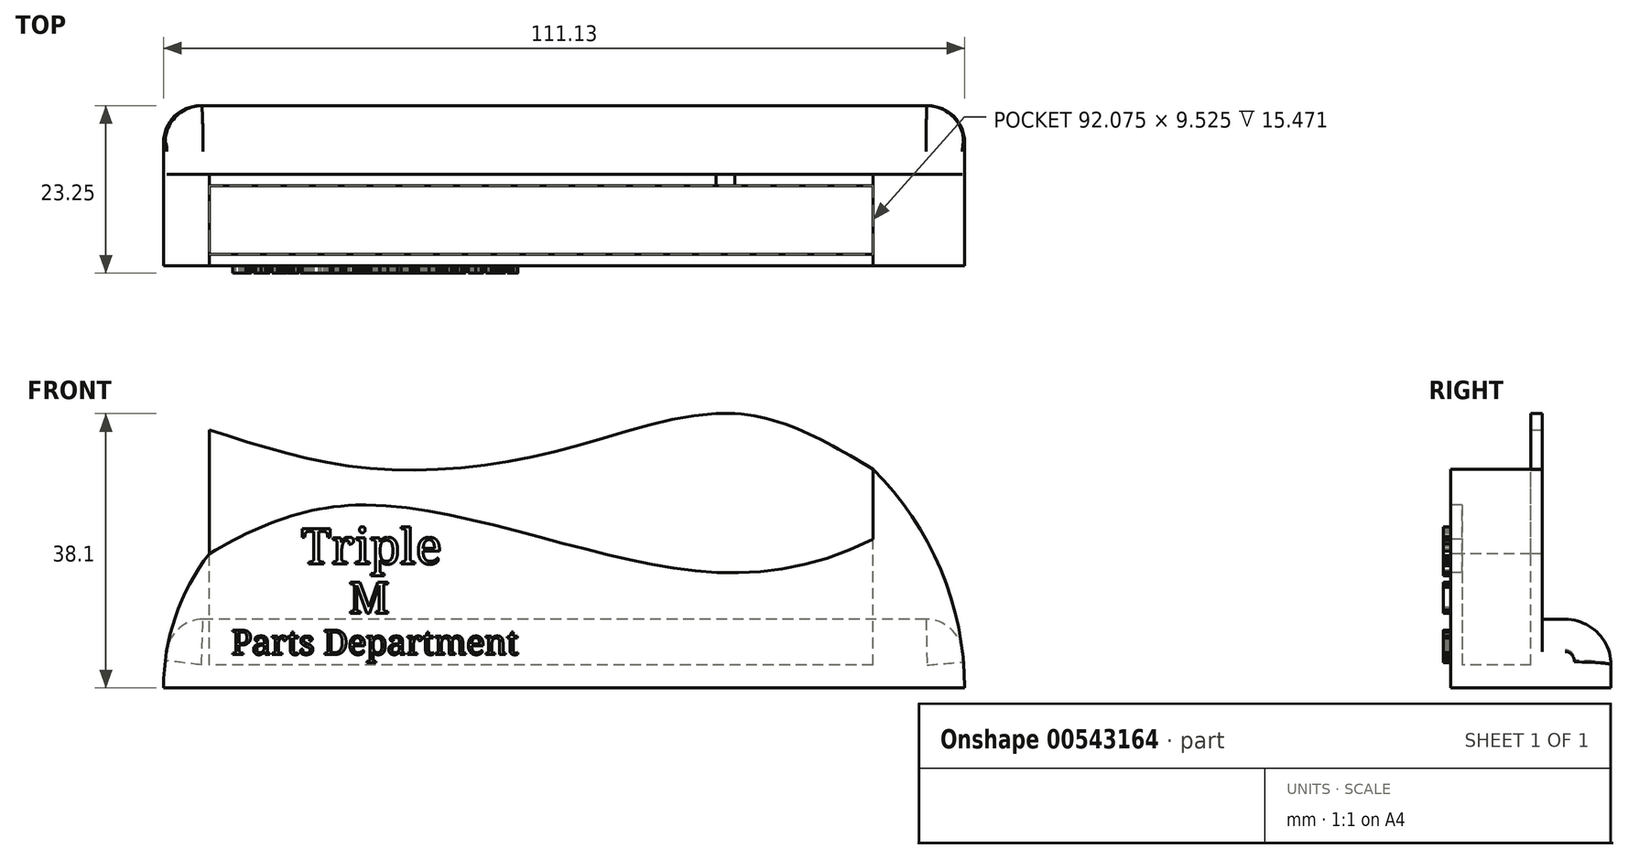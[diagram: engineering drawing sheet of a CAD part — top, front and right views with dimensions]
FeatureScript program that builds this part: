
annotation { "Feature Type Name" : "Feature", "Feature Type Description" : "" }
export const myFeature = defineFeature(function(context is Context, id is Id, definition is map)
    precondition{}
    {
        {
            var Q0;
            Q0=qCreatedBy(makeId("Right.planeOp"),FACE);
            var sketch = newSketch(context, id + "F0", { "sketchPlane" : qUnion([Q0])});
            skLineSegment(sketch, "E0", {"start": v(0, 0) * mm, "end": v(0, 25.4) * mm});
            skLineSegment(sketch, "E1", {"start": v(0, 25.4) * mm, "end": v(1.59, 25.4) * mm});
            skLineSegment(sketch, "E2", {"start": v(1.59, 25.4) * mm, "end": v(1.59, 3.18) * mm});
            skLineSegment(sketch, "E3", {"start": v(1.59, 3.18) * mm, "end": v(11.11, 3.18) * mm});
            skLineSegment(sketch, "E4", {"start": v(11.11, 3.18) * mm, "end": v(11.11, 38.1) * mm});
            skLineSegment(sketch, "E5", {"start": v(11.11, 38.1) * mm, "end": v(12.7, 38.1) * mm});
            skLineSegment(sketch, "E6", {"start": v(12.7, 38.1) * mm, "end": v(12.7, 0) * mm});
            skLineSegment(sketch, "E7", {"start": v(12.7, 0) * mm, "end": v(0, 0) * mm});
            skSolve(sketch);
        }
        {
            var Q0;
            Q0=makeQuery(id+"F0.imprint","IMPRINT",FACE,{"disambiguationData":[TD([[makeQuery(id+"F0.imprint","IMPRINT",EDGE,{"derivedFrom":sQuery(id+"F0.wireOp",EDGE,"E0")}),-1.0]])]});
            extrude(context, id + "F1", {"entities" : qUnion([Q0]), "depth" : 92.07 * mm});
        }
        {
            var Q0;
            Q0=makeQuery(id+"F1.opExtrude","SWEPT_FACE",FACE,{"disambiguationData":[OSD([sQuery(id+"F0.wireOp",EDGE,"E0")])]});
            var sketch = newSketch(context, id + "F2", { "sketchPlane" : qUnion([Q0])});
            skFitSpline(sketch, "E8", {"points": [v(0, 18.6) * mm, v(21.38, 25.4) * mm, v(56.78, 18.13) * mm, v(92.08, 20.65) * mm], "startDerivative": vector(67.88, 41.03) * mm, "endDerivative": vector(105.85, 52.89) * mm});
            skSolve(sketch);
        }
        {
            var Q0;
            {var subQ0=sQuery(id+"F0.wireOp",EDGE,"E0");var subQ1=makeQuery(id+"F1.opExtrude","CAP_EDGE",EDGE,{"disambiguationData":[OSD([subQ0])],"isStart":true});var subQ2=sQuery(id+"F2.wireOp",EDGE,"E8");var subQ3=makeQuery(id+"F2.imprint","INTERSECT",VERTEX,{"derivedFrom":[subQ1,subQ2]});Q0=makeQuery(id+"F2.imprint","IMPRINT",FACE,{"disambiguationData":[TD([[makeQuery(id+"F2.imprint","IMPRINT",EDGE,{"disambiguationData":[TD([[subQ3,-1.0]])],"derivedFrom":subQ2}),1.0]])]});}
            var Q1;
            {var subQ0=sQuery(id+"F0.wireOp",EDGE,"E0");var subQ1=makeQuery(id+"F1.opExtrude","CAP_EDGE",EDGE,{"disambiguationData":[OSD([subQ0])],"isStart":false});var subQ2=sQuery(id+"F2.wireOp",EDGE,"E8");var subQ3=makeQuery(id+"F2.imprint","INTERSECT",VERTEX,{"derivedFrom":[subQ1,subQ2]});Q1=makeQuery(id+"F2.imprint","IMPRINT",FACE,{"disambiguationData":[TD([[makeQuery(id+"F2.imprint","IMPRINT",EDGE,{"disambiguationData":[TD([[subQ3,1.0]])],"derivedFrom":subQ2}),1.0]])]});}
            extrude(context, id + "F3", {"entities" : qUnion([Q0, Q1]), "operationType" : NewBodyOperationType.REMOVE, "endBound" : BoundingType.UP_TO_NEXT, "oppositeDirection" : true, "depth" : 25.4 * mm});
        }
        {
            var Q0;
            Q0=makeQuery(id+"F1.opExtrude","SWEPT_FACE",FACE,{"disambiguationData":[OSD([sQuery(id+"F0.wireOp",EDGE,"E6")])]});
            var sketch = newSketch(context, id + "F4", { "sketchPlane" : qUnion([Q0])});
            skFitSpline(sketch, "E9", {"points": [v(-92.08, 30.36) * mm, v(-72.87, 38.1) * mm, v(-46.83, 32.53) * mm, v(-20.34, 30.7) * mm, v(0, 35.84) * mm], "startDerivative": vector(78.4, 47.13) * mm, "endDerivative": vector(83.06, 27.16) * mm});
            skSolve(sketch);
        }
        {
            var Q0;
            {var subQ0=sQuery(id+"F0.wireOp",EDGE,"E6");var subQ1=makeQuery(id+"F1.opExtrude","CAP_EDGE",EDGE,{"disambiguationData":[OSD([subQ0])],"isStart":false});var subQ2=sQuery(id+"F4.wireOp",EDGE,"E9");var subQ3=makeQuery(id+"F4.imprint","INTERSECT",VERTEX,{"derivedFrom":[subQ1,subQ2]});Q0=makeQuery(id+"F4.imprint","IMPRINT",FACE,{"disambiguationData":[TD([[makeQuery(id+"F4.imprint","IMPRINT",EDGE,{"disambiguationData":[TD([[subQ3,-1.0]])],"derivedFrom":subQ2}),1.0]])]});}
            var Q1;
            {var subQ0=sQuery(id+"F0.wireOp",EDGE,"E6");var subQ1=makeQuery(id+"F1.opExtrude","CAP_EDGE",EDGE,{"disambiguationData":[OSD([subQ0])],"isStart":true});var subQ2=sQuery(id+"F4.wireOp",EDGE,"E9");var subQ3=makeQuery(id+"F4.imprint","INTERSECT",VERTEX,{"derivedFrom":[subQ1,subQ2]});Q1=makeQuery(id+"F4.imprint","IMPRINT",FACE,{"disambiguationData":[TD([[makeQuery(id+"F4.imprint","IMPRINT",EDGE,{"disambiguationData":[TD([[subQ3,1.0]])],"derivedFrom":subQ2}),1.0]])]});}
            extrude(context, id + "F5", {"entities" : qUnion([Q0, Q1]), "operationType" : NewBodyOperationType.REMOVE, "endBound" : BoundingType.UP_TO_NEXT, "oppositeDirection" : true, "depth" : 25.4 * mm});
        }
        {
            var Q0;
            Q0=makeQuery(id+"F1.opExtrude","SWEPT_FACE",FACE,{"disambiguationData":[OSD([sQuery(id+"F0.wireOp",EDGE,"E0")])]});
            var sketch = newSketch(context, id + "F6", { "sketchPlane" : qUnion([Q0])});
            skLineSegment(sketch, "E10", {"start": v(46.04, 0) * mm, "end": v(46.04, 18.7) * mm, "construction": true});
            skSolve(sketch);
        }
        {
            var Q0;
            Q0=makeQuery(id+"F1.opExtrude","CAP_FACE",FACE,{"disambiguationData":[OSD([sQuery(id+"F0.wireOp",EDGE,"E0"),sQuery(id+"F0.wireOp",EDGE,"E1"),sQuery(id+"F0.wireOp",EDGE,"E2"),sQuery(id+"F0.wireOp",EDGE,"E3"),sQuery(id+"F0.wireOp",EDGE,"E4"),sQuery(id+"F0.wireOp",EDGE,"E5"),sQuery(id+"F0.wireOp",EDGE,"E6"),sQuery(id+"F0.wireOp",EDGE,"E7")])],"isStart":true});
            var sketch = newSketch(context, id + "F7", { "sketchPlane" : qUnion([Q0])});
            skLineSegment(sketch, "E11", {"start": v(-12.7, 3.18) * mm, "end": v(0, 3.17) * mm});
            skSolve(sketch);
        }
        {
            var Q0;
            {var subQ3=makeQuery(id+"F1.opExtrude","CAP_EDGE",EDGE,{"disambiguationData":[OSD([sQuery(id+"F0.wireOp",EDGE,"E7")])],"isStart":true});Q0=makeQuery(id+"F7.imprint","IMPRINT",FACE,{"disambiguationData":[TD([[makeQuery(id+"F7.imprint","IMPRINT",EDGE,{"derivedFrom":subQ3}),1.0]])]});}
            extrude(context, id + "F8", {"entities" : qUnion([Q0]), "operationType" : NewBodyOperationType.ADD, "depth" : 6.35 * mm});
        }
        {
            var Q0;
            Q0=makeQuery(id+"F8.boolean.opBoolean","MERGE",FACE,{"derivedFrom":[makeQuery(id+"F1.opExtrude","SWEPT_FACE",FACE,{"disambiguationData":[OSD([sQuery(id+"F0.wireOp",EDGE,"E3")])]}),makeQuery(id+"F8.opExtrude","SWEPT_FACE",FACE,{"disambiguationData":[OSD([sQuery(id+"F7.wireOp",EDGE,"E11")])]})]});
            var sketch = newSketch(context, id + "F9", { "sketchPlane" : qUnion([Q0])});
            skLineSegment(sketch, "E12", {"start": v(0, 11.11) * mm, "end": v(0, 1.59) * mm});
            skSolve(sketch);
        }
        {
            var Q0;
            Q0=makeQuery(id+"F9.imprint","IMPRINT",FACE,{"disambiguationData":[TD([[makeQuery(id+"F9.imprint","IMPRINT",EDGE,{"derivedFrom":sQuery(id+"F9.wireOp",EDGE,"E12")}),-1.0]])]});
            extrude(context, id + "F10", {"entities" : qUnion([Q0]), "operationType" : NewBodyOperationType.ADD, "depth" : 15.47 * mm});
        }
        {
            var Q0;
            {var subQ0=sQuery(id+"F0.wireOp",EDGE,"E0");var subQ1=sQuery(id+"F0.wireOp",EDGE,"E1");Q0=makeQuery(id+"F10.boolean.opBoolean","MERGE",FACE,{"derivedFrom":[makeQuery(id+"F8.boolean.opBoolean","MERGE",FACE,{"derivedFrom":[makeQuery(id+"FmbjE0y4cJYNi4l_1.boolean.opBoolean","SPLIT",FACE,{"disambiguationData":[TD([makeQuery(id+"F1.opExtrude","SWEPT_FACE",FACE,{"disambiguationData":[OSD([subQ1])]})])],"derivedFrom":makeQuery(id+"F1.opExtrude","SWEPT_FACE",FACE,{"disambiguationData":[OSD([subQ0])]})}),makeQuery(id+"F8.opExtrude","SWEPT_FACE",FACE,{"disambiguationData":[OSD([subQ0])]})]}),makeQuery(id+"F10.opExtrude","SWEPT_FACE",FACE,{"disambiguationData":[OSD([subQ0,sQuery(id+"F7.wireOp",EDGE,"E11")])]})]});}
            var sketch = newSketch(context, id + "F11", { "sketchPlane" : qUnion([Q0])});
            skArc(sketch, "E13", {"start": v(0, 18.65) * mm, "mid": v(-4.72, 9.85) * mm, "end": v(-6.35, 0) * mm});
            skSolve(sketch);
        }
        {
            var Q0;
            Q0=makeQuery(id+"F11.imprint","IMPRINT",FACE,{"disambiguationData":[TD([[makeQuery(id+"F11.imprint","IMPRINT",EDGE,{"derivedFrom":sQuery(id+"F11.wireOp",EDGE,"E13")}),-1.0]])]});
            extrude(context, id + "F12", {"entities" : qUnion([Q0]), "operationType" : NewBodyOperationType.REMOVE, "endBound" : BoundingType.UP_TO_NEXT, "oppositeDirection" : true, "depth" : 25.4 * mm});
        }
        {
            var Q0;
            Q0=makeQuery(id+"F1.opExtrude","CAP_FACE",FACE,{"disambiguationData":[OSD([sQuery(id+"F0.wireOp",EDGE,"E0"),sQuery(id+"F0.wireOp",EDGE,"E1"),sQuery(id+"F0.wireOp",EDGE,"E2"),sQuery(id+"F0.wireOp",EDGE,"E3"),sQuery(id+"F0.wireOp",EDGE,"E4"),sQuery(id+"F0.wireOp",EDGE,"E5"),sQuery(id+"F0.wireOp",EDGE,"E6"),sQuery(id+"F0.wireOp",EDGE,"E7")])],"isStart":false});
            var sketch = newSketch(context, id + "F13", { "sketchPlane" : qUnion([Q0])});
            skLineSegment(sketch, "E14", {"start": v(0, 20.65) * mm, "end": v(0, 30.36) * mm});
            skLineSegment(sketch, "E15", {"start": v(0, 30.36) * mm, "end": v(12.7, 30.36) * mm});
            skSolve(sketch);
        }
        {
            var Q0;
            Q0=makeQuery(id+"F13.imprint","IMPRINT",FACE,{"disambiguationData":[TD([[makeQuery(id+"F13.imprint","IMPRINT",EDGE,{"derivedFrom":makeQuery(id+"F1.opExtrude","CAP_EDGE",EDGE,{"disambiguationData":[OSD([sQuery(id+"F0.wireOp",EDGE,"E3")])],"isStart":false})}),-1.0]])]});
            var Q1;
            {var subQ4=sQuery(id+"F13.wireOp",EDGE,"E14");Q1=makeQuery(id+"F13.imprint","IMPRINT",FACE,{"disambiguationData":[TD([[makeQuery(id+"F13.imprint","IMPRINT",EDGE,{"derivedFrom":subQ4}),-1.0]])]});}
            extrude(context, id + "F14", {"entities" : qUnion([Q0, Q1]), "operationType" : NewBodyOperationType.ADD, "depth" : 12.7 * mm});
        }
        {
            var Q0;
            {var subQ0=sQuery(id+"F0.wireOp",EDGE,"E6");Q0=makeQuery(id+"F14.boolean.opBoolean","MERGE",FACE,{"derivedFrom":[makeQuery(id+"F10.boolean.opBoolean","MERGE",FACE,{"derivedFrom":[makeQuery(id+"F8.boolean.opBoolean","MERGE",FACE,{"derivedFrom":[makeQuery(id+"F1.opExtrude","SWEPT_FACE",FACE,{"disambiguationData":[OSD([subQ0])]}),makeQuery(id+"F8.opExtrude","SWEPT_FACE",FACE,{"disambiguationData":[OSD([subQ0])]})]}),makeQuery(id+"F10.opExtrude","SWEPT_FACE",FACE,{"disambiguationData":[OSD([subQ0,sQuery(id+"F7.wireOp",EDGE,"E11")])]})]}),makeQuery(id+"F14.opExtrude","SWEPT_FACE",FACE,{"disambiguationData":[OSD([subQ0])]})]});}
            var sketch = newSketch(context, id + "F15", { "sketchPlane" : qUnion([Q0])});
            skArc(sketch, "E16", {"start": v(-92.08, 30.36) * mm, "mid": v(-101.47, 16.46) * mm, "end": v(-104.78, 0) * mm});
            skSolve(sketch);
        }
        {
            var Q0;
            Q0=makeQuery(id+"F15.imprint","IMPRINT",FACE,{"disambiguationData":[TD([[makeQuery(id+"F15.imprint","IMPRINT",EDGE,{"derivedFrom":sQuery(id+"F15.wireOp",EDGE,"E16")}),-1.0]])]});
            extrude(context, id + "F16", {"entities" : qUnion([Q0]), "operationType" : NewBodyOperationType.REMOVE, "endBound" : BoundingType.UP_TO_NEXT, "oppositeDirection" : true, "depth" : 25.4 * mm});
        }
        {
            var Q0;
            {var subQ0=sQuery(id+"F0.wireOp",EDGE,"E6");Q0=makeQuery(id+"F14.boolean.opBoolean","MERGE",FACE,{"derivedFrom":[makeQuery(id+"F10.boolean.opBoolean","MERGE",FACE,{"derivedFrom":[makeQuery(id+"F8.boolean.opBoolean","MERGE",FACE,{"derivedFrom":[makeQuery(id+"F1.opExtrude","SWEPT_FACE",FACE,{"disambiguationData":[OSD([subQ0])]}),makeQuery(id+"F8.opExtrude","SWEPT_FACE",FACE,{"disambiguationData":[OSD([subQ0])]})]}),makeQuery(id+"F10.opExtrude","SWEPT_FACE",FACE,{"disambiguationData":[OSD([subQ0,sQuery(id+"F7.wireOp",EDGE,"E11")])]})]}),makeQuery(id+"F14.opExtrude","SWEPT_FACE",FACE,{"disambiguationData":[OSD([subQ0])]})]});}
            var sketch = newSketch(context, id + "F17", { "sketchPlane" : qUnion([Q0])});
            skLineSegment(sketch, "E17", {"start": v(-103.7, 9.53) * mm, "end": v(4.83, 9.53) * mm});
            skSolve(sketch);
        }
        {
            var Q0;
            {var subQ1=sQuery(id+"F17.wireOp",EDGE,"E17");Q0=makeQuery(id+"F17.imprint","IMPRINT",FACE,{"disambiguationData":[TD([[makeQuery(id+"F17.imprint","IMPRINT",EDGE,{"derivedFrom":subQ1}),-1.0]])]});}
            extrude(context, id + "F18", {"entities" : qUnion([Q0]), "operationType" : NewBodyOperationType.ADD, "depth" : 9.52 * mm});
        }
        {
            var Q0;
            Q0=makeQuery(id+"F18.opExtrude","CAP_EDGE",EDGE,{"disambiguationData":[OSD([sQuery(id+"F17.wireOp",EDGE,"E17")])],"isStart":false});
            fillet(context, id + "F19", {"entities" : qUnion([Q0]), "radius" : 6.35 * mm, "tangentPropagation" : true, "allowEdgeOverflow" : false});
        }
        {
            var Q0;
            {var subQ0=sQuery(id+"F15.wireOp",EDGE,"E16");Q0=makeQuery(id+"F19.opFillet","BLEND_EDGE",EDGE,{"blendedFrom":[makeQuery(id+"F18.opExtrude","CAP_EDGE",EDGE,{"disambiguationData":[OSD([sQuery(id+"F17.wireOp",EDGE,"E17")])],"isStart":false}),makeQuery(id+"F18.boolean.opBoolean","MERGE",FACE,{"derivedFrom":[makeQuery(id+"F16.boolean.opBoolean","COPY",FACE,{"derivedFrom":makeQuery(id+"F16.opExtrude","SWEPT_FACE",FACE,{"disambiguationData":[OSD([subQ0])]})}),makeQuery(id+"F18.opExtrude","SWEPT_FACE",FACE,{"disambiguationData":[OSD([subQ0])]})]})],"blendedInto":[makeQuery(id+"F18.boolean.opBoolean","MERGE",FACE,{"derivedFrom":[makeQuery(id+"F16.boolean.opBoolean","COPY",FACE,{"derivedFrom":makeQuery(id+"F16.opExtrude","SWEPT_FACE",FACE,{"disambiguationData":[OSD([subQ0])]})}),makeQuery(id+"F18.opExtrude","SWEPT_FACE",FACE,{"disambiguationData":[OSD([subQ0])]})]})]});}
            var Q1;
            {var subQ0=sQuery(id+"F11.wireOp",EDGE,"E13");Q1=makeQuery(id+"F19.opFillet","BLEND_EDGE",EDGE,{"blendedFrom":[makeQuery(id+"F18.opExtrude","CAP_EDGE",EDGE,{"disambiguationData":[OSD([sQuery(id+"F17.wireOp",EDGE,"E17")])],"isStart":false}),makeQuery(id+"F18.boolean.opBoolean","MERGE",FACE,{"derivedFrom":[makeQuery(id+"F12.boolean.opBoolean","COPY",FACE,{"derivedFrom":makeQuery(id+"F12.opExtrude","SWEPT_FACE",FACE,{"disambiguationData":[OSD([subQ0])]})}),makeQuery(id+"F18.opExtrude","SWEPT_FACE",FACE,{"disambiguationData":[OSD([sQuery(id+"F0.wireOp",EDGE,"E6"),sQuery(id+"F7.wireOp",EDGE,"E11"),subQ0])]})]})],"blendedInto":[makeQuery(id+"F18.boolean.opBoolean","MERGE",FACE,{"derivedFrom":[makeQuery(id+"F12.boolean.opBoolean","COPY",FACE,{"derivedFrom":makeQuery(id+"F12.opExtrude","SWEPT_FACE",FACE,{"disambiguationData":[OSD([subQ0])]})}),makeQuery(id+"F18.opExtrude","SWEPT_FACE",FACE,{"disambiguationData":[OSD([sQuery(id+"F0.wireOp",EDGE,"E6"),sQuery(id+"F7.wireOp",EDGE,"E11"),subQ0])]})]})]});}
            fillet(context, id + "F20", {"entities" : qUnion([Q0, Q1]), "radius" : 5.08 * mm, "tangentPropagation" : true, "allowEdgeOverflow" : false});
        }
        {
            var Q0;
            {var subQ0=sQuery(id+"F0.wireOp",EDGE,"E0");var subQ4=makeQuery(id+"F1.opExtrude","CAP_EDGE",EDGE,{"disambiguationData":[OSD([subQ0])],"isStart":true});Q0=makeQuery(id+"F6.imprint","IMPRINT",FACE,{"disambiguationData":[TD([[makeQuery(id+"F6.imprint","IMPRINT",EDGE,{"derivedFrom":subQ4}),-1.0]])]});}
            var sketch = newSketch(context, id + "F21", { "sketchPlane" : qUnion([Q0])});
            skText(sketch, "E18", { "text": "M", "fontName": "NotoSerif-Regular.ttf"});
            skText(sketch, "E19", { "text": "Parts Department ", "fontName": "NotoSerif-Regular.ttf"});
            skText(sketch, "E20", { "text": "Triple", "fontName": "NotoSerif-Regular.ttf"});
            const initialGuessF21  = {"E18": [0.0193, 0.01037, 1, 0, 0.00435], "E19": [0.00305, 0.00464, 1, 0, 0.0034], "E20": [0.01274, 0.01721, 1, 0, 0.00491]};
            skSetInitialGuess(sketch, initialGuessF21);
            skSolve(sketch);
        }
        {
            var Q0;
            Q0 = qSketchRegion(id + "F21", true);
            extrude(context, id + "F22", {"entities" : qUnion([Q0]), "operationType" : NewBodyOperationType.ADD, "depth" : 1.02 * mm, "offsetDistance" : 25.4 * mm});
        }
    });
